# Revit family: 303_R15X_
name_source: partatom
category: Pipe Accessories
revit_build: Autodesk Revit 2018 (Build: 20170223_1515(x64)
units: mm (PartAtom-declared; Revit-internal decimal feet)

## family parameters
Always vertical = Yes
Cut with Voids When Loaded = No
Part Type = Valve - Breaks Into
Round Connector Dimension = Use Diameter
Shared = No
Work Plane-Based = No

## types (5) — shared parameters
CAT0 = Yes
Description = Straight lockshild valve
J6 = 18 mm  [stored 0.0590551 ft]
L2D_Min = 3048 mm
Manufacturer = Giacomini
QmdConnectorList = 301;D;302;D1
RS1 = No
URL = http://www.giacomini.com
magiPartTypeId = 303
magiProductFamilyId = R15X*
zero-valued in all types: MC_Default_elevation

## per-type parameters (varying)
- R15X032: B3=9 mm  [stored 0.0295276 ft]; B4=6 mm  [stored 0.019685 ft]; CenSd_K2_6=10 mm  [stored 0.0328084 ft]; CenSd_W2_6=12 mm  [stored 0.0393701 ft]; D=10 mm; D1=10 mm; G1=8 mm  [stored 0.0262467 ft]; G3=10 mm  [stored 0.0328084 ft]; J5=2 mm  [stored 0.00656168 ft]; K2=11 mm  [stored 0.0360892 ft]; K3=9 mm  [stored 0.0295276 ft]; L2=9 mm  [stored 0.0295276 ft]; L2D=58 mm; L4=7 mm  [stored 0.0229659 ft]; L5=9 mm  [stored 0.0295276 ft]; L6=4 mm  [stored 0.0131234 ft]; L62=2 mm  [stored 0.00656168 ft]; L62__ve=-2 mm  [stored -0.00656168 ft]; L6__ve=-4 mm  [stored -0.0131234 ft]; L8=2 mm  [stored 0.00656168 ft]; L8__ve=-2 mm  [stored -0.00656168 ft]; L9=7 mm  [stored 0.0229659 ft]; L9__ve=-7 mm; LC=51 mm; LC1=29 mm  [stored 0.0951444 ft]; LC2=48 mm; LX=29 mm  [stored 0.0951444 ft]; M1=18 mm  [stored 0.0590551 ft]; M11=21 mm  [stored 0.0688976 ft]; M12=11 mm  [stored 0.0360892 ft]; R1=8 mm  [stored 0.0262467 ft]; RS=Yes; RS2=Yes; RS3=No; SW1=Yes; SW2=No; W2=14 mm  [stored 0.0459318 ft]; W2D=10 mm  [stored 0.0328084 ft]; W4=8 mm  [stored 0.0262467 ft]; X11=13 mm
- R15X036: B3=18 mm  [stored 0.0590551 ft]; B4=11 mm  [stored 0.0360892 ft]; CenSd_K2_6=21 mm  [stored 0.0688976 ft]; CenSd_W2_6=23 mm; D=32 mm; D1=32 mm; G1=19 mm  [stored 0.062336 ft]; G3=21 mm  [stored 0.0688976 ft]; J5=15 mm  [stored 0.0492126 ft]; K2=25 mm  [stored 0.082021 ft]; K3=20 mm  [stored 0.0656168 ft]; L2=14 mm  [stored 0.0459318 ft]; L2D=89 mm; L4=10 mm  [stored 0.0328084 ft]; L5=14 mm  [stored 0.0459318 ft]; L6=7 mm  [stored 0.0229659 ft]; L62=3 mm  [stored 0.00984252 ft]; L62__ve=-3 mm; L6__ve=-7 mm; L8=3 mm  [stored 0.00984252 ft]; L8__ve=-3 mm; L9=10 mm  [stored 0.0328084 ft]; L9__ve=-10 mm  [stored -0.0328084 ft]; LC=79 mm; LC1=45 mm; LC2=74 mm; LX=48 mm; M1=23 mm; M11=27 mm; M12=20 mm  [stored 0.0656168 ft]; R1=19 mm  [stored 0.062336 ft]; RS=No; RS2=No; RS3=Yes; SW1=No; SW2=Yes; W2=27 mm; W2D=32 mm; W4=16 mm  [stored 0.0524934 ft]; X11=21 mm  [stored 0.0688976 ft]
- R15X035: B3=16 mm  [stored 0.0524934 ft]; B4=10 mm  [stored 0.0328084 ft]; CenSd_K2_6=17 mm; CenSd_W2_6=20 mm  [stored 0.0656168 ft]; D=25 mm; D1=25 mm; G1=15 mm  [stored 0.0492126 ft]; G3=17 mm; J5=14 mm  [stored 0.0459318 ft]; K2=20 mm  [stored 0.0656168 ft]; K3=16 mm  [stored 0.0524934 ft]; L2=12 mm  [stored 0.0393701 ft]; L2D=80 mm; L4=9 mm  [stored 0.0295276 ft]; L5=12 mm  [stored 0.0393701 ft]; L6=6 mm  [stored 0.019685 ft]; L62=3 mm  [stored 0.00984252 ft]; L62__ve=-3 mm; L6__ve=-6 mm; L8=3 mm  [stored 0.00984252 ft]; L8__ve=-3 mm; L9=9 mm  [stored 0.0295276 ft]; L9__ve=-9 mm; LC=69 mm; LC1=40 mm; LC2=67 mm; LX=42 mm  [stored 0.137795 ft]; M1=20 mm  [stored 0.0656168 ft]; M11=24 mm; M12=17 mm; R1=16 mm  [stored 0.0524934 ft]; RS=No; RS2=No; RS3=Yes; SW1=No; SW2=Yes; W2=23 mm; W2D=25 mm  [stored 0.082021 ft]; W4=14 mm  [stored 0.0459318 ft]; X11=18 mm  [stored 0.0590551 ft]
- R15X034: B3=13 mm; B4=8 mm  [stored 0.0262467 ft]; CenSd_K2_6=14 mm  [stored 0.0459318 ft]; CenSd_W2_6=16 mm  [stored 0.0524934 ft]; D=20 mm; D1=20 mm; G1=13 mm; G3=15 mm  [stored 0.0492126 ft]; J5=6 mm  [stored 0.019685 ft]; K2=16 mm  [stored 0.0524934 ft]; K3=13 mm; L2=9 mm  [stored 0.0295276 ft]; L2D=61 mm; L4=7 mm  [stored 0.0229659 ft]; L5=9 mm  [stored 0.0295276 ft]; L6=5 mm  [stored 0.0164042 ft]; L62=2 mm  [stored 0.00656168 ft]; L62__ve=-2 mm  [stored -0.00656168 ft]; L6__ve=-5 mm  [stored -0.0164042 ft]; L8=2 mm  [stored 0.00656168 ft]; L8__ve=-2 mm  [stored -0.00656168 ft]; L9=7 mm  [stored 0.0229659 ft]; L9__ve=-7 mm; LC=55 mm; LC1=31 mm; LC2=51 mm; LX=31 mm; M1=18 mm  [stored 0.0590551 ft]; M11=21 mm  [stored 0.0688976 ft]; M12=14 mm  [stored 0.0459318 ft]; R1=13 mm; RS=No; RS2=No; RS3=Yes; SW1=No; SW2=Yes; W2=19 mm  [stored 0.062336 ft]; W2D=20 mm  [stored 0.0656168 ft]; W4=11 mm  [stored 0.0360892 ft]; X11=14 mm  [stored 0.0459318 ft]
- R15X033: B3=10 mm  [stored 0.0328084 ft]; B4=7 mm  [stored 0.0229659 ft]; CenSd_K2_6=11 mm  [stored 0.0360892 ft]; CenSd_W2_6=13 mm; D=15 mm; D1=15 mm; G1=10 mm  [stored 0.0328084 ft]; G3=12 mm  [stored 0.0393701 ft]; J5=3 mm  [stored 0.00984252 ft]; K2=13 mm; K3=10 mm  [stored 0.0328084 ft]; L2=9 mm  [stored 0.0295276 ft]; L2D=57 mm; L4=7 mm  [stored 0.0229659 ft]; L5=9 mm  [stored 0.0295276 ft]; L6=4 mm  [stored 0.0131234 ft]; L62=2 mm  [stored 0.00656168 ft]; L62__ve=-2 mm  [stored -0.00656168 ft]; L6__ve=-4 mm  [stored -0.0131234 ft]; L8=2 mm  [stored 0.00656168 ft]; L8__ve=-2 mm  [stored -0.00656168 ft]; L9=7 mm  [stored 0.0229659 ft]; L9__ve=-7 mm; LC=52 mm; LC1=29 mm  [stored 0.0951444 ft]; LC2=48 mm; LX=28 mm; M1=18 mm  [stored 0.0590551 ft]; M11=21 mm  [stored 0.0688976 ft]; M12=11 mm  [stored 0.0360892 ft]; R1=11 mm  [stored 0.0360892 ft]; RS=Yes; RS2=Yes; RS3=No; SW1=Yes; SW2=No; W2=15 mm  [stored 0.0492126 ft]; W2D=15 mm  [stored 0.0492126 ft]; W4=9 mm  [stored 0.0295276 ft]; X11=13 mm

note: column(s) folded — value = type name in every type: magiProductCode, magiProductId

note: [stored X ft] marks values corroborated as IEEE doubles in the binary element streams (Revit-internal decimal feet)

## geometry (parser evidence)
native form markers: Sweep x1
no freeform markers — native parametric forms only
